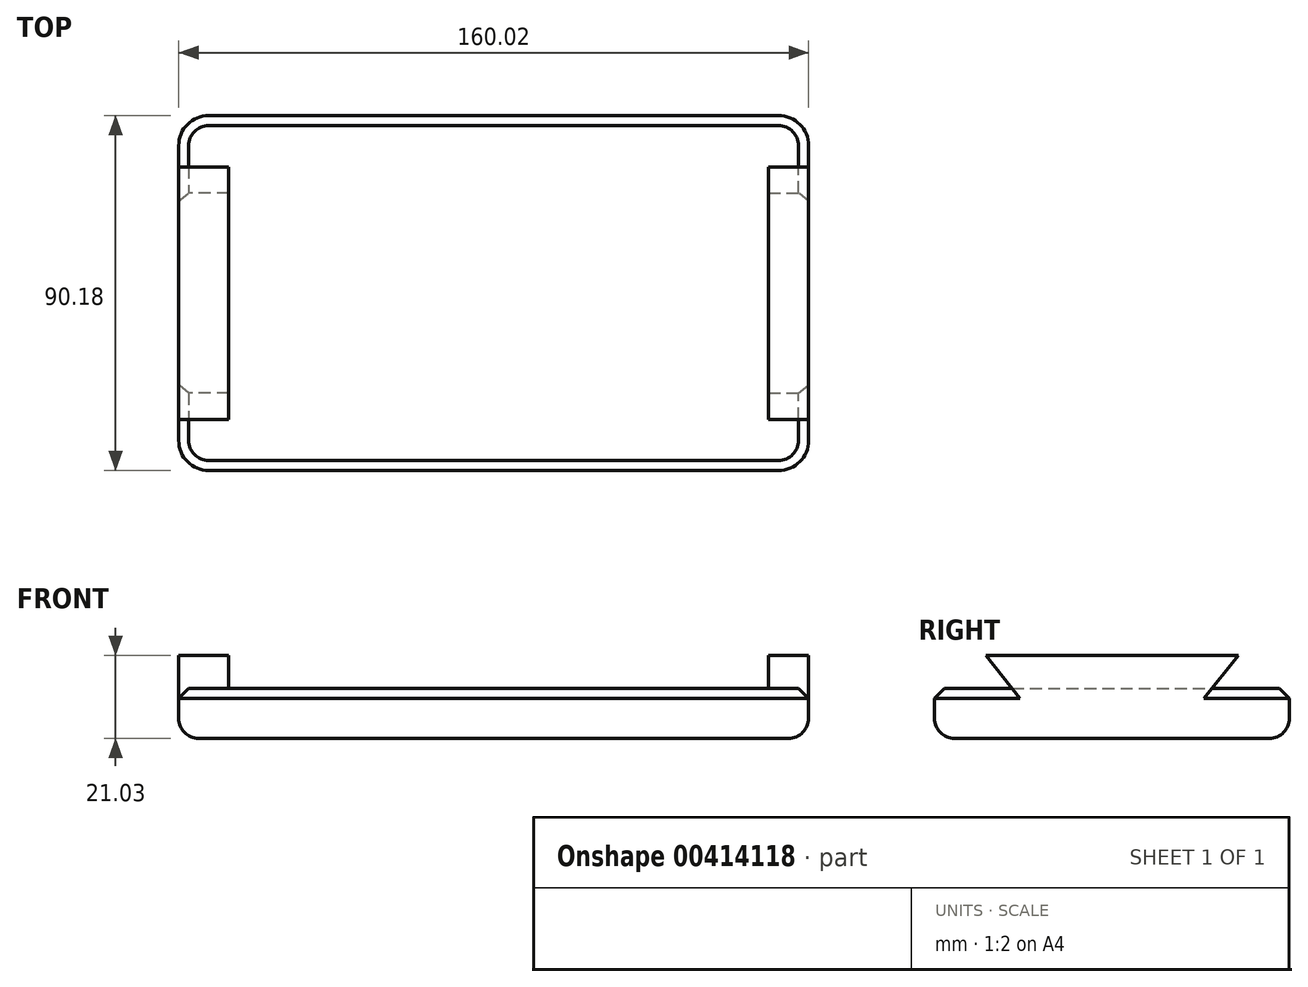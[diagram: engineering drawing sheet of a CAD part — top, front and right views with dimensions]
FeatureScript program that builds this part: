
annotation { "Feature Type Name" : "Feature", "Feature Type Description" : "" }
export const myFeature = defineFeature(function(context is Context, id is Id, definition is map)
    precondition{}
    {
        {
            var Q0;
            Q0=qCreatedBy(makeId("Top.planeOp"),FACE);
            var sketch = newSketch(context, id + "F0", { "sketchPlane" : qUnion([Q0])});
            skLineSegment(sketch, "E0.bottom", {"start": v(74.93, -40) * mm, "end": v(-74.93, -40) * mm});
            skLineSegment(sketch, "E0.top", {"start": v(74.93, 40) * mm, "end": v(-74.93, 40) * mm});
            skLineSegment(sketch, "E0.left", {"start": v(74.93, -40) * mm, "end": v(74.93, 40) * mm});
            skLineSegment(sketch, "E0.right", {"start": v(-74.93, -40) * mm, "end": v(-74.93, 40) * mm});
            skPoint(sketch, "E0.middle", {"position": v(0, 0) * mm});
            skLineSegment(sketch, "E1.bottom", {"start": v(-80.01, -45.09) * mm, "end": v(80.01, -45.09) * mm});
            skLineSegment(sketch, "E1.top", {"start": v(-80.01, 45.09) * mm, "end": v(80.01, 45.09) * mm});
            skLineSegment(sketch, "E1.left", {"start": v(-80.01, -45.09) * mm, "end": v(-80.01, 45.09) * mm});
            skLineSegment(sketch, "E1.right", {"start": v(80.01, -45.09) * mm, "end": v(80.01, 45.09) * mm});
            skSolve(sketch);
        }
        {
            var Q0;
            Q0=makeQuery(id+"F0.imprint","IMPRINT",FACE,{"disambiguationData":[TD([[makeQuery(id+"F0.imprint","IMPRINT",EDGE,{"derivedFrom":sQuery(id+"F0.wireOp",EDGE,"E0.bottom")}),-1.0]])]});
            extrude(context, id + "F1", {"entities" : qUnion([Q0]), "depth" : 12.7 * mm});
        }
        {
            var Q0;
            Q0=makeQuery(id+"F0.imprint","IMPRINT",FACE,{"disambiguationData":[TD([[makeQuery(id+"F0.imprint","IMPRINT",EDGE,{"derivedFrom":sQuery(id+"F0.wireOp",EDGE,"E0.bottom")}),1.0]])]});
            extrude(context, id + "F2", {"entities" : qUnion([Q0]), "operationType" : NewBodyOperationType.ADD, "depth" : 12.7 * mm});
        }
        {
            var Q0;
            Q0=makeQuery(id+"F2.opExtrude","SWEPT_EDGE",EDGE,{"disambiguationData":[OSD([sQuery(id+"F0.wireOp",EDGE,"E1.top"),sQuery(id+"F0.wireOp",EDGE,"E1.left")])]});
            var Q1;
            Q1=makeQuery(id+"F2.opExtrude","SWEPT_EDGE",EDGE,{"disambiguationData":[OSD([sQuery(id+"F0.wireOp",EDGE,"E1.bottom"),sQuery(id+"F0.wireOp",EDGE,"E1.left")])]});
            var Q2;
            Q2=makeQuery(id+"F2.opExtrude","SWEPT_EDGE",EDGE,{"disambiguationData":[OSD([sQuery(id+"F0.wireOp",EDGE,"E1.bottom"),sQuery(id+"F0.wireOp",EDGE,"E1.right")])]});
            var Q3;
            Q3=makeQuery(id+"F2.opExtrude","SWEPT_EDGE",EDGE,{"disambiguationData":[OSD([sQuery(id+"F0.wireOp",EDGE,"E1.top"),sQuery(id+"F0.wireOp",EDGE,"E1.right")])]});
            fillet(context, id + "F3", {"entities" : qUnion([Q0, Q1, Q2, Q3]), "radius" : 7.62 * mm, "tangentPropagation" : true, "allowEdgeOverflow" : false});
        }
        {
            var Q0;
            Q0=makeQuery(id+"F2.opExtrude","CAP_EDGE",EDGE,{"disambiguationData":[OSD([sQuery(id+"F0.wireOp",EDGE,"E1.left")])],"isStart":true});
            var Q1;
            Q1=makeQuery(id+"F2.opExtrude","CAP_EDGE",EDGE,{"disambiguationData":[OSD([sQuery(id+"F0.wireOp",EDGE,"E1.top")])],"isStart":true});
            var Q2;
            Q2=makeQuery(id+"F2.opExtrude","CAP_EDGE",EDGE,{"disambiguationData":[OSD([sQuery(id+"F0.wireOp",EDGE,"E1.right")])],"isStart":true});
            var Q3;
            {var subQ0=sQuery(id+"F0.wireOp",EDGE,"E1.right");var subQ1=sQuery(id+"F0.wireOp",EDGE,"E1.top");var subQ2=sQuery(id+"F0.wireOp",EDGE,"E0.right");var subQ3=sQuery(id+"F0.wireOp",EDGE,"E0.left");var subQ4=sQuery(id+"F0.wireOp",EDGE,"E0.top");var subQ5=sQuery(id+"F0.wireOp",EDGE,"E0.bottom");Q3=makeQuery(id+"F3.opFillet","BLEND_EDGE",EDGE,{"blendedFrom":[makeQuery(id+"F2.opExtrude","SWEPT_EDGE",EDGE,{"disambiguationData":[OSD([subQ1,subQ0])]}),makeQuery(id+"F2.boolean.opBoolean","MERGE",FACE,{"derivedFrom":[makeQuery(id+"F1.opExtrude","CAP_FACE",FACE,{"disambiguationData":[OSD([subQ5,subQ4,subQ3,subQ2])],"isStart":true}),makeQuery(id+"F2.opExtrude","CAP_FACE",FACE,{"disambiguationData":[OSD([subQ5,subQ4,subQ3,subQ2,sQuery(id+"F0.wireOp",EDGE,"E1.bottom"),subQ1,sQuery(id+"F0.wireOp",EDGE,"E1.left"),subQ0])],"isStart":true})]})],"blendedInto":[makeQuery(id+"F2.boolean.opBoolean","MERGE",FACE,{"derivedFrom":[makeQuery(id+"F1.opExtrude","CAP_FACE",FACE,{"disambiguationData":[OSD([subQ5,subQ4,subQ3,subQ2])],"isStart":true}),makeQuery(id+"F2.opExtrude","CAP_FACE",FACE,{"disambiguationData":[OSD([subQ5,subQ4,subQ3,subQ2,sQuery(id+"F0.wireOp",EDGE,"E1.bottom"),subQ1,sQuery(id+"F0.wireOp",EDGE,"E1.left"),subQ0])],"isStart":true})]})]});}
            var Q4;
            {var subQ0=sQuery(id+"F0.wireOp",EDGE,"E1.right");var subQ1=sQuery(id+"F0.wireOp",EDGE,"E1.bottom");var subQ2=sQuery(id+"F0.wireOp",EDGE,"E0.right");var subQ3=sQuery(id+"F0.wireOp",EDGE,"E0.left");var subQ4=sQuery(id+"F0.wireOp",EDGE,"E0.top");var subQ5=sQuery(id+"F0.wireOp",EDGE,"E0.bottom");Q4=makeQuery(id+"F3.opFillet","BLEND_EDGE",EDGE,{"blendedFrom":[makeQuery(id+"F2.opExtrude","SWEPT_EDGE",EDGE,{"disambiguationData":[OSD([subQ1,subQ0])]}),makeQuery(id+"F2.boolean.opBoolean","MERGE",FACE,{"derivedFrom":[makeQuery(id+"F1.opExtrude","CAP_FACE",FACE,{"disambiguationData":[OSD([subQ5,subQ4,subQ3,subQ2])],"isStart":true}),makeQuery(id+"F2.opExtrude","CAP_FACE",FACE,{"disambiguationData":[OSD([subQ5,subQ4,subQ3,subQ2,subQ1,sQuery(id+"F0.wireOp",EDGE,"E1.top"),sQuery(id+"F0.wireOp",EDGE,"E1.left"),subQ0])],"isStart":true})]})],"blendedInto":[makeQuery(id+"F2.boolean.opBoolean","MERGE",FACE,{"derivedFrom":[makeQuery(id+"F1.opExtrude","CAP_FACE",FACE,{"disambiguationData":[OSD([subQ5,subQ4,subQ3,subQ2])],"isStart":true}),makeQuery(id+"F2.opExtrude","CAP_FACE",FACE,{"disambiguationData":[OSD([subQ5,subQ4,subQ3,subQ2,subQ1,sQuery(id+"F0.wireOp",EDGE,"E1.top"),sQuery(id+"F0.wireOp",EDGE,"E1.left"),subQ0])],"isStart":true})]})]});}
            var Q5;
            {var subQ0=sQuery(id+"F0.wireOp",EDGE,"E1.left");var subQ1=sQuery(id+"F0.wireOp",EDGE,"E1.bottom");var subQ2=sQuery(id+"F0.wireOp",EDGE,"E0.right");var subQ3=sQuery(id+"F0.wireOp",EDGE,"E0.left");var subQ4=sQuery(id+"F0.wireOp",EDGE,"E0.top");var subQ5=sQuery(id+"F0.wireOp",EDGE,"E0.bottom");Q5=makeQuery(id+"F3.opFillet","BLEND_EDGE",EDGE,{"blendedFrom":[makeQuery(id+"F2.opExtrude","SWEPT_EDGE",EDGE,{"disambiguationData":[OSD([subQ1,subQ0])]}),makeQuery(id+"F2.boolean.opBoolean","MERGE",FACE,{"derivedFrom":[makeQuery(id+"F1.opExtrude","CAP_FACE",FACE,{"disambiguationData":[OSD([subQ5,subQ4,subQ3,subQ2])],"isStart":true}),makeQuery(id+"F2.opExtrude","CAP_FACE",FACE,{"disambiguationData":[OSD([subQ5,subQ4,subQ3,subQ2,subQ1,sQuery(id+"F0.wireOp",EDGE,"E1.top"),subQ0,sQuery(id+"F0.wireOp",EDGE,"E1.right")])],"isStart":true})]})],"blendedInto":[makeQuery(id+"F2.boolean.opBoolean","MERGE",FACE,{"derivedFrom":[makeQuery(id+"F1.opExtrude","CAP_FACE",FACE,{"disambiguationData":[OSD([subQ5,subQ4,subQ3,subQ2])],"isStart":true}),makeQuery(id+"F2.opExtrude","CAP_FACE",FACE,{"disambiguationData":[OSD([subQ5,subQ4,subQ3,subQ2,subQ1,sQuery(id+"F0.wireOp",EDGE,"E1.top"),subQ0,sQuery(id+"F0.wireOp",EDGE,"E1.right")])],"isStart":true})]})]});}
            var Q6;
            Q6=makeQuery(id+"F2.opExtrude","CAP_EDGE",EDGE,{"disambiguationData":[OSD([sQuery(id+"F0.wireOp",EDGE,"E1.bottom")])],"isStart":true});
            fillet(context, id + "F4", {"entities" : qUnion([Q0, Q1, Q2, Q3, Q4, Q5, Q6]), "radius" : 5.08 * mm, "tangentPropagation" : true, "allowEdgeOverflow" : false});
        }
        {
            var Q0;
            {var subQ0=sQuery(id+"F0.wireOp",EDGE,"E0.right");var subQ1=sQuery(id+"F0.wireOp",EDGE,"E0.left");var subQ2=sQuery(id+"F0.wireOp",EDGE,"E0.top");var subQ3=sQuery(id+"F0.wireOp",EDGE,"E0.bottom");Q0=makeQuery(id+"F2.boolean.opBoolean","MERGE",FACE,{"derivedFrom":[makeQuery(id+"F1.opExtrude","CAP_FACE",FACE,{"disambiguationData":[OSD([subQ3,subQ2,subQ1,subQ0])],"isStart":false}),makeQuery(id+"F2.opExtrude","CAP_FACE",FACE,{"disambiguationData":[OSD([subQ3,subQ2,subQ1,subQ0,sQuery(id+"F0.wireOp",EDGE,"E1.bottom"),sQuery(id+"F0.wireOp",EDGE,"E1.top"),sQuery(id+"F0.wireOp",EDGE,"E1.left"),sQuery(id+"F0.wireOp",EDGE,"E1.right")])],"isStart":false})]});}
            var sketch = newSketch(context, id + "F5", { "sketchPlane" : qUnion([Q0])});
            skLineSegment(sketch, "E2", {"start": v(80.01, 0) * mm, "end": v(80.01, -25.4) * mm});
            skLineSegment(sketch, "E3", {"start": v(80.01, -25.4) * mm, "end": v(80.01, 11.86) * mm});
            skLineSegment(sketch, "E4", {"start": v(80.01, -25.4) * mm, "end": v(80.01, 25.4) * mm});
            skLineSegment(sketch, "E5.MirrorCS", {"start": v(-80.01, -25.4) * mm, "end": v(-80.01, 11.86) * mm});
            skLineSegment(sketch, "E6.MirrorCS", {"start": v(-80.01, 0) * mm, "end": v(-80.01, -25.4) * mm});
            skLineSegment(sketch, "E7.MirrorCS", {"start": v(-80.01, -25.4) * mm, "end": v(-80.01, 25.4) * mm});
            skSolve(sketch);
        }
        {
            var Q0;
            Q0=sQuery(id+"F5.wireOp",EDGE,"E7.MirrorCS");
            var Q1;
            Q1=sQuery(id+"F5.wireOp",EDGE,"E4");
            extrude(context, id + "F6", {"bodyType" : ToolBodyType.SURFACE, "surfaceEntities" : qUnion([Q0, Q1]), "depth" : 6.35 * mm});
        }
        {
            var Q0;
            Q0=makeQuery(id+"F6.opExtrude","SWEPT_FACE",FACE,{"disambiguationData":[OSD([sQuery(id+"F5.wireOp",EDGE,"E7.MirrorCS")])]});
            var sketch = newSketch(context, id + "F7", { "sketchPlane" : qUnion([Q0])});
            skLineSegment(sketch, "E8", {"start": v(-32.06, 21.03) * mm, "end": v(-25.4, 12.7) * mm});
            skLineSegment(sketch, "E9", {"start": v(32.07, 21.03) * mm, "end": v(25.4, 12.7) * mm});
            skLineSegment(sketch, "E10", {"start": v(32.07, 21.03) * mm, "end": v(-32.06, 21.03) * mm});
            skSolve(sketch);
        }
        {
            var Q0;
            Q0=makeQuery(id+"F7.imprint","IMPRINT",FACE,{"disambiguationData":[TD([[makeQuery(id+"F7.imprint","IMPRINT",EDGE,{"derivedFrom":sQuery(id+"F7.wireOp",EDGE,"NBWbgQ19-HUtt-10bA-x5dZ-YNA0YoKxYoTH")}),-1.0]])]});
            var Q1;
            Q1=makeQuery(id+"F7.imprint","IMPRINT",FACE,{"disambiguationData":[TD([[makeQuery(id+"F7.imprint","IMPRINT",EDGE,{"derivedFrom":makeQuery(id+"F6.opExtrude","SWEPT_EDGE",EDGE,{"disambiguationData":[OSD([sQuery(id+"F5.wireOp",VERTEX,"E7.MirrorCS.start")])]})}),-1.0]])]});
            var Q2;
            Q2=makeQuery(id+"F7.imprint","IMPRINT",FACE,{"disambiguationData":[TD([[makeQuery(id+"F7.imprint","IMPRINT",EDGE,{"derivedFrom":sQuery(id+"F7.wireOp",EDGE,"KR5gv6Jb-7ykD-I6iA-3cSO-UOI6GFVYMw72")}),1.0]])]});
            var Q3;
            Q3=makeQuery(id+"F7.imprint","IMPRINT",FACE,{"disambiguationData":[TD([[makeQuery(id+"F7.imprint","IMPRINT",EDGE,{"derivedFrom":sQuery(id+"F7.wireOp",EDGE,"E8")}),1.0]])]});
            extrude(context, id + "F8", {"entities" : qUnion([Q0, Q1, Q2, Q3]), "operationType" : NewBodyOperationType.ADD, "depth" : 12.7 * mm});
        }
        {
            var Q0;
            Q0=makeQuery(id+"F6.opExtrude","SWEPT_FACE",FACE,{"disambiguationData":[OSD([sQuery(id+"F5.wireOp",EDGE,"E4")])]});
            var sketch = newSketch(context, id + "F9", { "sketchPlane" : qUnion([Q0])});
            skLineSegment(sketch, "E11", {"start": v(-32.06, 21.03) * mm, "end": v(-25.4, 12.7) * mm});
            skLineSegment(sketch, "E12", {"start": v(32.07, 21.03) * mm, "end": v(25.4, 12.7) * mm});
            skLineSegment(sketch, "E13", {"start": v(32.07, 21.03) * mm, "end": v(-32.06, 21.03) * mm});
            skSolve(sketch);
        }
        {
            var Q0;
            Q0=makeQuery(id+"F9.imprint","IMPRINT",FACE,{"disambiguationData":[TD([[makeQuery(id+"F9.imprint","IMPRINT",EDGE,{"derivedFrom":sQuery(id+"F9.wireOp",EDGE,"c1n0gpVT-FrPd-1Pyy-zCPP-xo0KbSA4SsKh")}),-1.0]])]});
            var Q1;
            Q1=makeQuery(id+"F9.imprint","IMPRINT",FACE,{"disambiguationData":[TD([[makeQuery(id+"F9.imprint","IMPRINT",EDGE,{"derivedFrom":makeQuery(id+"F6.opExtrude","SWEPT_EDGE",EDGE,{"disambiguationData":[OSD([sQuery(id+"F5.wireOp",VERTEX,"E4.start")])]})}),-1.0]])]});
            var Q2;
            Q2=makeQuery(id+"F9.imprint","IMPRINT",FACE,{"disambiguationData":[TD([[makeQuery(id+"F9.imprint","IMPRINT",EDGE,{"derivedFrom":sQuery(id+"F9.wireOp",EDGE,"ewVmiKBG-zjFw-HFB3-P6UY-vT6gvt8bIbUG")}),1.0]])]});
            var Q3;
            Q3=makeQuery(id+"F9.imprint","IMPRINT",FACE,{"disambiguationData":[TD([[makeQuery(id+"F9.imprint","IMPRINT",EDGE,{"derivedFrom":sQuery(id+"F9.wireOp",EDGE,"E11")}),1.0]])]});
            extrude(context, id + "F10", {"entities" : qUnion([Q0, Q1, Q2, Q3]), "operationType" : NewBodyOperationType.ADD, "oppositeDirection" : true, "depth" : 10.16 * mm});
        }
        {
            var Q0;
            Q0=makeQuery(id+"F2.opExtrude","CAP_EDGE",EDGE,{"disambiguationData":[OSD([sQuery(id+"F0.wireOp",EDGE,"E1.top")])],"isStart":false});
            var Q1;
            Q1=makeQuery(id+"F2.opExtrude","CAP_EDGE",EDGE,{"disambiguationData":[OSD([sQuery(id+"F0.wireOp",EDGE,"E1.bottom")])],"isStart":false});
            chamfer(context, id + "F11", {"entities" : qUnion([Q0, Q1]), "width" : 2.54 * mm, "tangentPropagation" : true});
        }
    });
